# Revit family: Führungsklammer-Set, Typ 4A
name_source: partatom
category: HLS-Bauteile
revit_build: Autodesk Revit 2018 (Build: 20190510_1515(x64)
units: mm (PartAtom-declared; Revit-internal decimal feet)

## family parameters
Arbeitsebenenbasiert = Ja
Beim Laden mit Abzugskörper schneiden = Nein
Bemaßung runder Anschluss = Durchmesser verwenden
Gemeinsam genutzt = Ja
Immer vertikal = Nein
Raumberechnungspunkt = Nein
Teiletyp = Normal

## types (1)
- Führungsklammer Set Typ 2A mit Abheb. mit Gleitunt., Typ 4A III
    Artikelnummer = 14710007
    Fabrikat = MEFA
    Faktor1 = 115 mm  [stored 0.377297 ft]
    Firma = MEFA Befestigungs- und Montagesysteme GmbH
    Gewicht = 2.75 kg
    Gewicht pro Bauteil = 2.75 kg
    Gewindestangentyp = M12 x 310
    Klemmweite = HEA 200, HEB180-200, IPE360-400, IPEa400-450
    Klemmweite Flansch max. = 200 mm  [stored 0.656168 ft]
    Klemmweite Flansch min. = 170 mm  [stored 0.557743 ft]
    Kurztext1 = Führungsklammer-Set mit Abhebesicherung und Gleitunterlage
    Kurztext2 = Typ 4A III Klemmdicke 10 - 15 mm
    Material = Stahl
    Materialname = S235
    Mengeneinheit = St
    Oberflaeche = feuerstückverzinkt
    Typ = 4A III
    Vorgabe-Ansicht = 1219 mm
    max. zul. Last Zug = 3.50 kN
    max. zul. Schublast = 4.00 kN
    min. Klemmdicke = 10 mm
    vpe = 1 St

note: [stored X ft] marks values corroborated as IEEE doubles in the binary element streams (Revit-internal decimal feet)

## geometry (parser evidence)
native form markers: Sweep x3
no freeform markers — native parametric forms only
